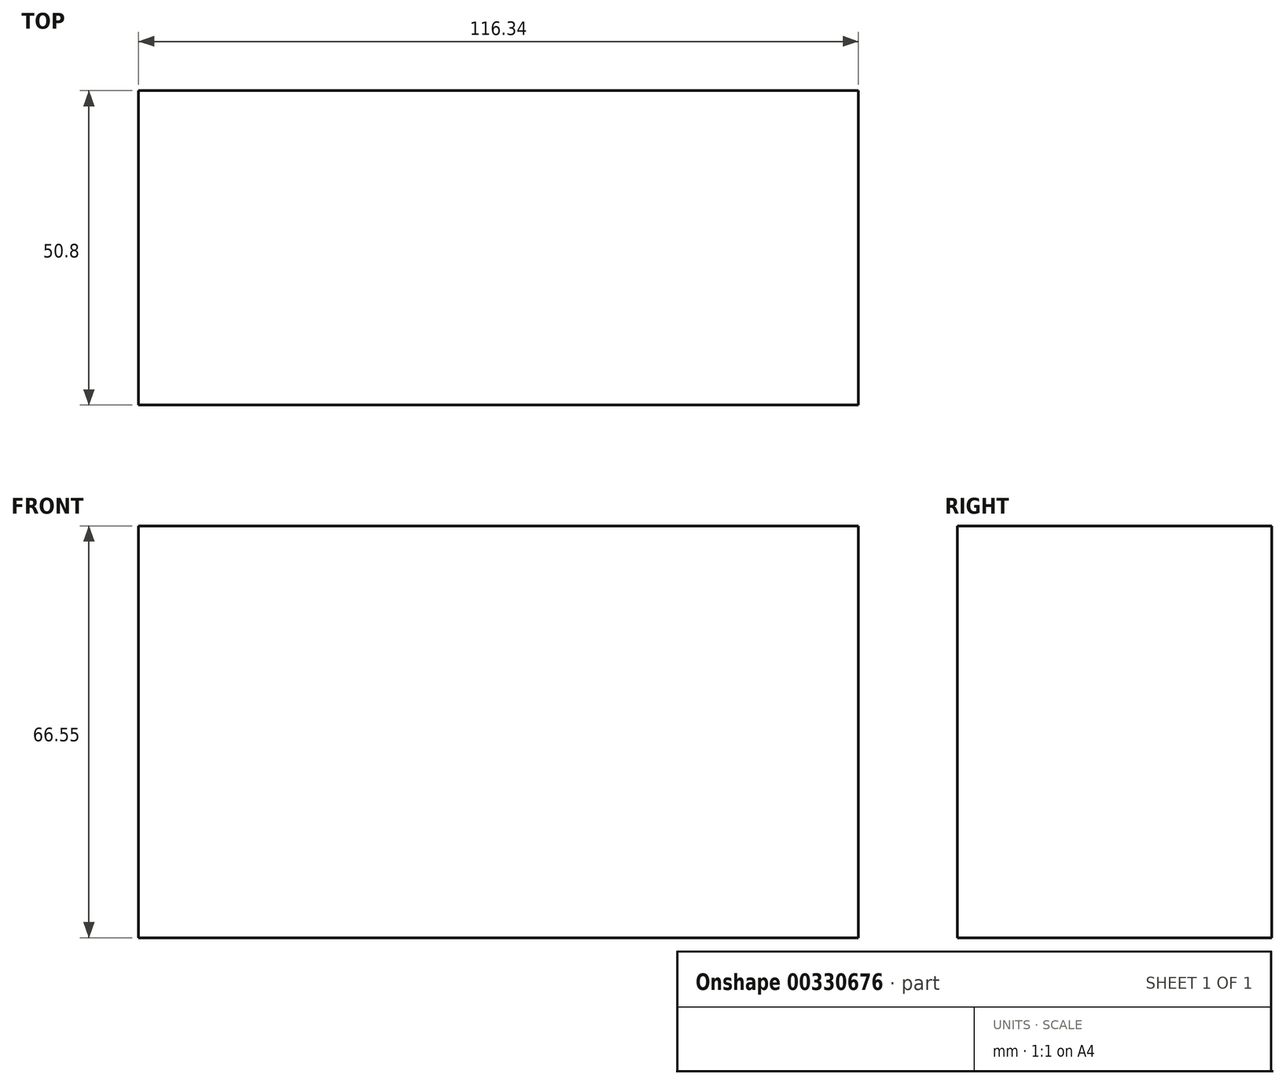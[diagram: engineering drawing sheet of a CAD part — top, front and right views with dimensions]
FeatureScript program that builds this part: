
annotation { "Feature Type Name" : "Feature", "Feature Type Description" : "" }
export const myFeature = defineFeature(function(context is Context, id is Id, definition is map)
    precondition{}
    {
        {
            var Q0;
            Q0=qCreatedBy(makeId("Front.planeOp"),FACE);
            var sketch = newSketch(context, id + "F0", { "sketchPlane" : qUnion([Q0])});
            skLineSegment(sketch, "E0.bottom", {"start": v(-76.19, 66.55) * mm, "end": v(40.15, 66.55) * mm});
            skLineSegment(sketch, "E0.top", {"start": v(-76.19, 0) * mm, "end": v(40.15, 0) * mm});
            skLineSegment(sketch, "E0.left", {"start": v(-76.19, 66.55) * mm, "end": v(-76.19, 0) * mm});
            skLineSegment(sketch, "E0.right", {"start": v(40.15, 66.55) * mm, "end": v(40.15, 0) * mm});
            skSolve(sketch);
        }
        {
            var Q0;
            Q0=makeQuery(id+"F0.imprint","IMPRINT",FACE,{"disambiguationData":[TD([[makeQuery(id+"F0.imprint","IMPRINT",EDGE,{"derivedFrom":sQuery(id+"F0.wireOp",EDGE,"E0.bottom")}),-1.0]])]});
            extrude(context, id + "F1", {"entities" : qUnion([Q0]), "depth" : 50.8 * mm});
        }
    });
